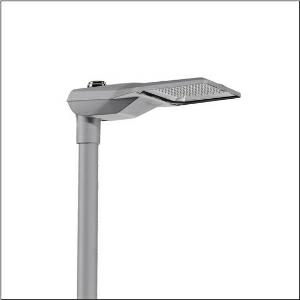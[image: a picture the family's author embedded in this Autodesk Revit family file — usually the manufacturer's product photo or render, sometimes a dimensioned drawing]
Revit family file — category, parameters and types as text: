
# Revit family: streetlight_sl_21_midi___pl52_5xe7h47n08lb_ccfd
name_source: partatom
category: Lighting Fixtures
units: mm (PartAtom-declared; Revit-internal decimal feet)

## family parameters
Cut with Voids When Loaded = No
Host = Face
Light Source = No
Part Type = Normal
Room Calculation Point = No
Round Connector Dimension = Use Diameter
Shared = No

## types (1)
- --- (1 x LED, 14690 lm, 98.3 W, 4000K)
    Apparent Load = 98 VA
    CIE Flux Codes = 27 59 98 100 100
    Color Rendering = 70
    Color Temperature = 4000K
    Default Elevation = 1800 mm
    Description = Streetlight SL 21 midi, mast luminaire, primary light control with lens, of PMMA, primary optical cover: cover, of toughened safety glass, transparent, light distribution: PL52, light emission: direct distribution, primary light characteristic: asymmetric, installation type: side-entry, LED, 3G 2.5mm², High Power LED, rated luminous flux: 14.690lm, luminous efficacy: 149lm/W, light colour: 740, colour temperature: 4000K, control gear: NEMA (7pin), control: overheat protection, pre-setting: linear dimming characteristic, constant luminous flux control, time-dependent luminous flux control, flexible luminous flux parameterisation, mains connection: 220..240V, AC, 50/60Hz, connection cable pre-assembled, cable length: 10,5m, wiring characteristics: H05VV-F, start of lifetime: 98W, end of service life: 101W, reduction: 45W, luminaire housing, of diecast aluminium (EN AC-44300), powder-coated, Siteco® metallic grey (DB 702S), corrosivity category C5 mid according to DIN EN ISO 12944, multi-level sealing system, sealing non-destructively replaceable, inclination adjustable: 0°, 5°, 10°, 15°, length: 644mm, width: 335mm, height: 110mm, spigot size: 42mm (side-entry), mounting height: 4..8m, protection rating (complete): IP66, insulation class (complete): insulation class I (protective earthing), certification: CE, ENEC, ENEC+, VDE, impact resistance: IK10, permissible operating ambient temperature for outdoor applications: -40..+50°C, standard-compliant lighting for roads and squares, packaging unit: 1 piece

Light Distribution: PL52
    Height = 111 mm
    Lamp = 1 x LED
    Lamp Light Flux = 14690 lm
    Lamp Power = 98.3 W
    Lamp count = 1
    Length = 644 mm
    Luminous efficacy = 149 lm/W
    Manufacturer = Siteco
    ModVariant = No
    Model = 5XE7H47N08LB
    Number of Poles = 1
    OnlyDefault = Yes
    Power Factor = 1
    Product Name = Streetlight SL 21 midi | PL52
    Product group = mast luminaire | pylon top
    ProductGroupID = 6100
    Protection Class = Protection class I
    Protection Degree = IP 66
    RLX_Detail_Level = 1
    RLX_Emergency_Light_Flux = 0 lm
    RLX_Emergency_Type = 0
    RLX_Emergency_Type_DB = No
    RlxData = <blob elided: 36329 chars, md5=7bae749a>
    Socket = socket
    Standby Power = 0 W
    System Light Flux = 14690 lm
    System Power = 98 W
    Type Comments = factory setting: luminous flux: 100 % | dim-lin: 254 | 1020 mA
    Type Image = l_1294377.jpg
    URL = http://relux.com
    VarID = @adj_136848
    Voltage = 0 V
    Weight = 0.00 kg
    Width = 336 mm

## geometry (parser evidence)
native form markers: Blend x4, Sweep x11
no freeform markers — native parametric forms only
